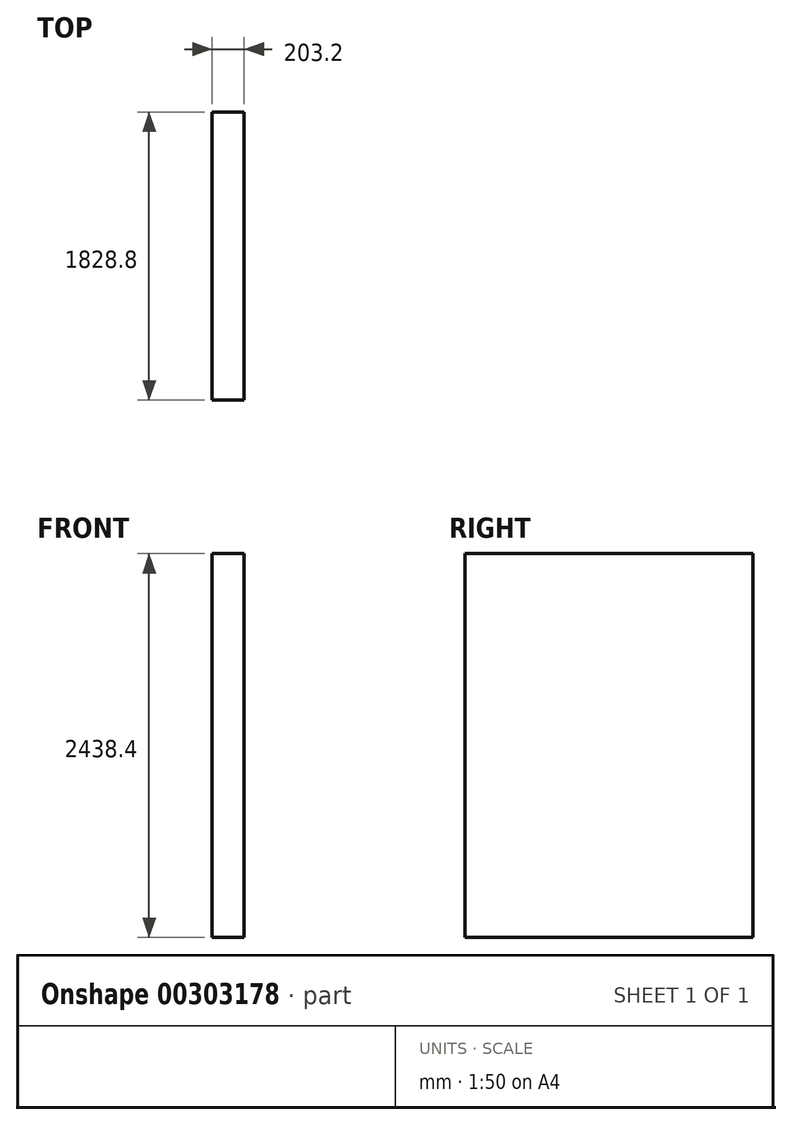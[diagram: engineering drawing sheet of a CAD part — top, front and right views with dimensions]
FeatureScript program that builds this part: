
annotation { "Feature Type Name" : "Feature", "Feature Type Description" : "" }
export const myFeature = defineFeature(function(context is Context, id is Id, definition is map)
    precondition{}
    {
        {
            var Q0;
            Q0=qCreatedBy(makeId("Top.planeOp"),FACE);
            var sketch = newSketch(context, id + "F0", { "sketchPlane" : qUnion([Q0])});
            skLineSegment(sketch, "E0.bottom", {"start": v(101.6, 914.4) * mm, "end": v(-101.6, 914.4) * mm});
            skLineSegment(sketch, "E0.top", {"start": v(101.6, -914.4) * mm, "end": v(-101.6, -914.4) * mm});
            skLineSegment(sketch, "E0.left", {"start": v(101.6, 914.4) * mm, "end": v(101.6, -914.4) * mm});
            skLineSegment(sketch, "E0.right", {"start": v(-101.6, 914.4) * mm, "end": v(-101.6, -914.4) * mm});
            skPoint(sketch, "E0.middle", {"position": v(0, 0) * mm});
            skSolve(sketch);
        }
        {
            var Q0;
            Q0=makeQuery(id+"F0.imprint","IMPRINT",FACE,{"disambiguationData":[TD([[makeQuery(id+"F0.imprint","IMPRINT",EDGE,{"derivedFrom":sQuery(id+"F0.wireOp",EDGE,"E0.bottom")}),1.0]])]});
            extrude(context, id + "F1", {"entities" : qUnion([Q0]), "depth" : 2438.4 * mm});
        }
    });
